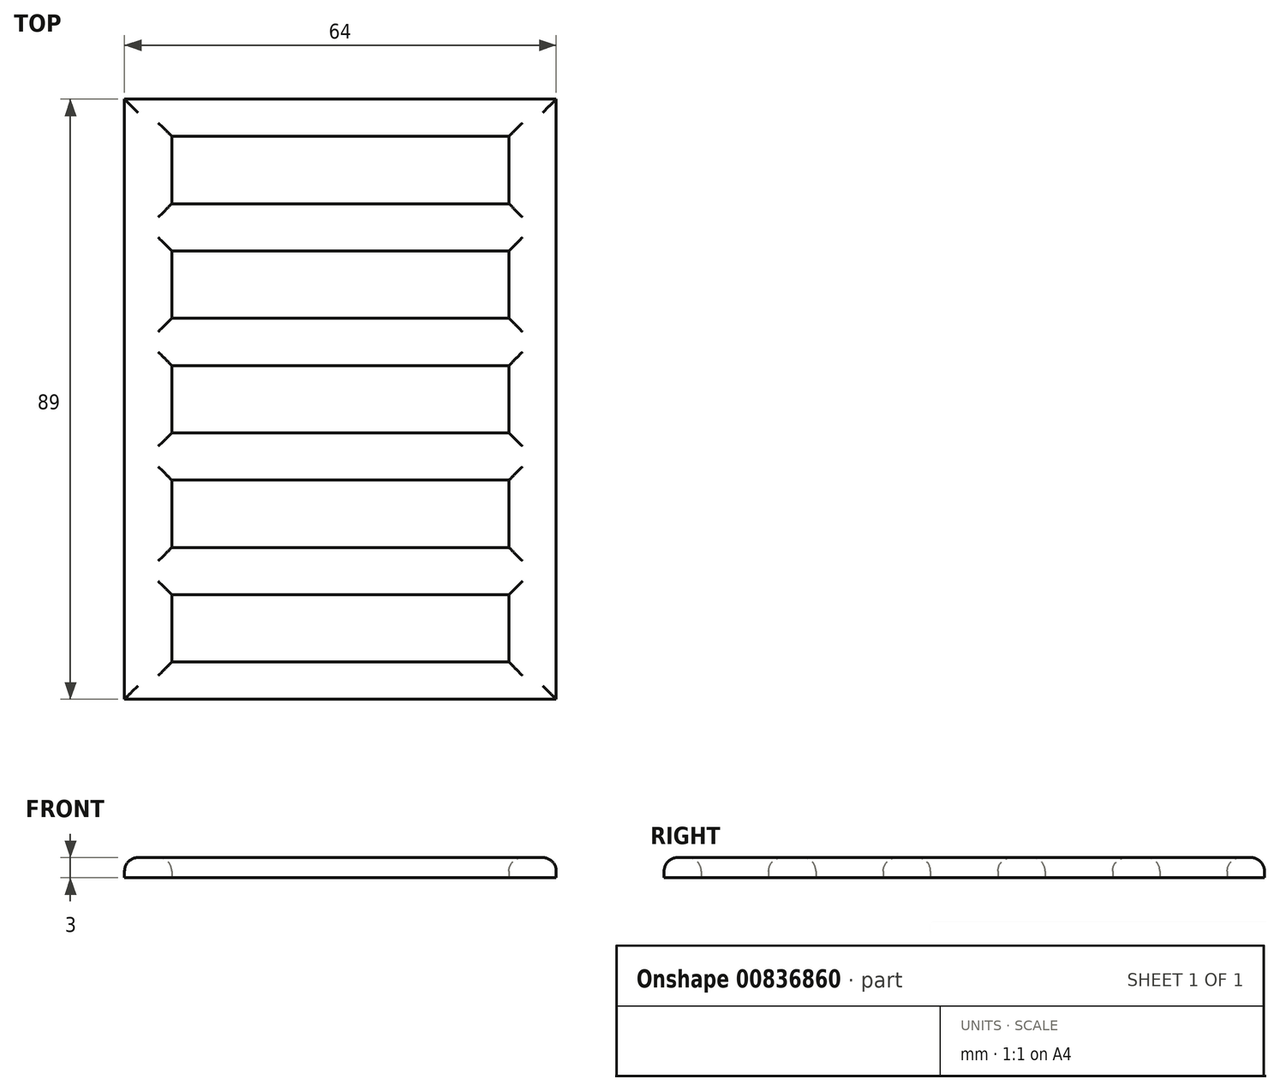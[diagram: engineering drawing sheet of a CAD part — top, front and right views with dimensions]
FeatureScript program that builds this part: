
annotation { "Feature Type Name" : "Feature", "Feature Type Description" : "" }
export const myFeature = defineFeature(function(context is Context, id is Id, definition is map)
    precondition{}
    {
        {
            var Q0;
            Q0=qCreatedBy(makeId("Top.planeOp"),FACE);
            var sketch = newSketch(context, id + "F0", { "sketchPlane" : qUnion([Q0])});
            skLineSegment(sketch, "E0.bottom", {"start": v(0, 0) * mm, "end": v(-64, 0) * mm});
            skLineSegment(sketch, "E0.top", {"start": v(0, 89) * mm, "end": v(-64, 89) * mm});
            skLineSegment(sketch, "E0.left", {"start": v(0, 0) * mm, "end": v(0, 89) * mm});
            skLineSegment(sketch, "E0.right", {"start": v(-64, 0) * mm, "end": v(-64, 89) * mm});
            skLineSegment(sketch, "E1.0", {"start": v(-0.1, 88.9) * mm, "end": v(-63.9, 88.9) * mm});
            skLineSegment(sketch, "E1.1", {"start": v(-0.1, 0.1) * mm, "end": v(-0.1, 88.9) * mm});
            skLineSegment(sketch, "E1.2", {"start": v(-0.1, 0.1) * mm, "end": v(-63.9, 0.1) * mm});
            skLineSegment(sketch, "E1.3", {"start": v(-63.9, 0.1) * mm, "end": v(-63.9, 88.9) * mm});
            skLineSegment(sketch, "E2", {"start": v(-63.9, 88.9) * mm, "end": v(-0.1, 0.1) * mm, "construction": true});
            skLineSegment(sketch, "E3.bottom", {"start": v(-7, 49.5) * mm, "end": v(-57, 49.5) * mm});
            skLineSegment(sketch, "E3.top", {"start": v(-7, 39.5) * mm, "end": v(-57, 39.5) * mm});
            skLineSegment(sketch, "E3.left", {"start": v(-7, 49.5) * mm, "end": v(-7, 39.5) * mm});
            skLineSegment(sketch, "E3.right", {"start": v(-57, 49.5) * mm, "end": v(-57, 39.5) * mm});
            skPoint(sketch, "E3.middle", {"position": v(-32, 44.5) * mm});
            skLineSegment(sketch, "E4", {"start": v(-32, 44.5) * mm, "end": v(-32, 61.5) * mm, "construction": true});
            skLineSegment(sketch, "E5", {"start": v(-32, 61.5) * mm, "end": v(-32, 78.5) * mm, "construction": true});
            skLineSegment(sketch, "E6", {"start": v(-32, 44.5) * mm, "end": v(-32, 27.5) * mm, "construction": true});
            skLineSegment(sketch, "E7", {"start": v(-32, 27.5) * mm, "end": v(-32, 10.5) * mm, "construction": true});
            skLineSegment(sketch, "E8.bottom", {"start": v(-7, 56.5) * mm, "end": v(-57, 56.5) * mm});
            skLineSegment(sketch, "E8.top", {"start": v(-7, 66.5) * mm, "end": v(-57, 66.5) * mm});
            skLineSegment(sketch, "E8.left", {"start": v(-7, 56.5) * mm, "end": v(-7, 66.5) * mm});
            skLineSegment(sketch, "E8.right", {"start": v(-57, 56.5) * mm, "end": v(-57, 66.5) * mm});
            skPoint(sketch, "E8.middle", {"position": v(-32, 61.5) * mm});
            skLineSegment(sketch, "E9.bottom", {"start": v(-7, 73.5) * mm, "end": v(-57, 73.5) * mm});
            skLineSegment(sketch, "E9.top", {"start": v(-7, 83.5) * mm, "end": v(-57, 83.5) * mm});
            skLineSegment(sketch, "E9.left", {"start": v(-7, 73.5) * mm, "end": v(-7, 83.5) * mm});
            skLineSegment(sketch, "E9.right", {"start": v(-57, 73.5) * mm, "end": v(-57, 83.5) * mm});
            skPoint(sketch, "E9.middle", {"position": v(-32, 78.5) * mm});
            skLineSegment(sketch, "E10.bottom", {"start": v(-57, 32.5) * mm, "end": v(-7, 32.5) * mm});
            skLineSegment(sketch, "E10.top", {"start": v(-57, 22.5) * mm, "end": v(-7, 22.5) * mm});
            skLineSegment(sketch, "E10.left", {"start": v(-57, 32.5) * mm, "end": v(-57, 22.5) * mm});
            skLineSegment(sketch, "E10.right", {"start": v(-7, 32.5) * mm, "end": v(-7, 22.5) * mm});
            skPoint(sketch, "E10.middle", {"position": v(-32, 27.5) * mm});
            skLineSegment(sketch, "E11.bottom", {"start": v(-57, 15.5) * mm, "end": v(-7, 15.5) * mm});
            skLineSegment(sketch, "E11.top", {"start": v(-57, 5.5) * mm, "end": v(-7, 5.5) * mm});
            skLineSegment(sketch, "E11.left", {"start": v(-57, 15.5) * mm, "end": v(-57, 5.5) * mm});
            skLineSegment(sketch, "E11.right", {"start": v(-7, 15.5) * mm, "end": v(-7, 5.5) * mm});
            skPoint(sketch, "E11.middle", {"position": v(-32, 10.5) * mm});
            skSolve(sketch);
        }
        {
            var Q0;
            Q0=makeQuery(id+"F0.imprint","IMPRINT",FACE,{"disambiguationData":[TD([[makeQuery(id+"F0.imprint","IMPRINT",EDGE,{"derivedFrom":sQuery(id+"F0.wireOp",EDGE,"E1.0")}),1.0]])]});
            var Q1;
            Q1=makeQuery(id+"F0.imprint","IMPRINT",FACE,{"disambiguationData":[TD([[makeQuery(id+"F0.imprint","IMPRINT",EDGE,{"derivedFrom":sQuery(id+"F0.wireOp",EDGE,"E0.bottom")}),-1.0]])]});
            extrude(context, id + "F1", {"entities" : qUnion([Q0, Q1]), "depth" : 3 * mm, "offsetDistance" : 25 * mm});
        }
        {
            var Q0;
            Q0=makeQuery(id+"F1.opExtrude","CAP_FACE",FACE,{"disambiguationData":[OSD([sQuery(id+"F0.wireOp",EDGE,"E0.bottom"),sQuery(id+"F0.wireOp",EDGE,"E0.top"),sQuery(id+"F0.wireOp",EDGE,"E0.left"),sQuery(id+"F0.wireOp",EDGE,"E0.right"),sQuery(id+"F0.wireOp",EDGE,"E3.bottom"),sQuery(id+"F0.wireOp",EDGE,"E3.top"),sQuery(id+"F0.wireOp",EDGE,"E3.left"),sQuery(id+"F0.wireOp",EDGE,"E3.right"),sQuery(id+"F0.wireOp",EDGE,"E8.bottom"),sQuery(id+"F0.wireOp",EDGE,"E8.top"),sQuery(id+"F0.wireOp",EDGE,"E8.left"),sQuery(id+"F0.wireOp",EDGE,"E8.right"),sQuery(id+"F0.wireOp",EDGE,"E9.bottom"),sQuery(id+"F0.wireOp",EDGE,"E9.top"),sQuery(id+"F0.wireOp",EDGE,"E9.left"),sQuery(id+"F0.wireOp",EDGE,"E9.right"),sQuery(id+"F0.wireOp",EDGE,"E10.bottom"),sQuery(id+"F0.wireOp",EDGE,"E10.top"),sQuery(id+"F0.wireOp",EDGE,"E10.left"),sQuery(id+"F0.wireOp",EDGE,"E10.right"),sQuery(id+"F0.wireOp",EDGE,"E11.bottom"),sQuery(id+"F0.wireOp",EDGE,"E11.top"),sQuery(id+"F0.wireOp",EDGE,"E11.left"),sQuery(id+"F0.wireOp",EDGE,"E11.right")])],"isStart":false});
            fillet(context, id + "F2", {"entities" : qUnion([Q0]), "radius" : 2 * mm, "tangentPropagation" : true, "allowEdgeOverflow" : false});
        }
    });
